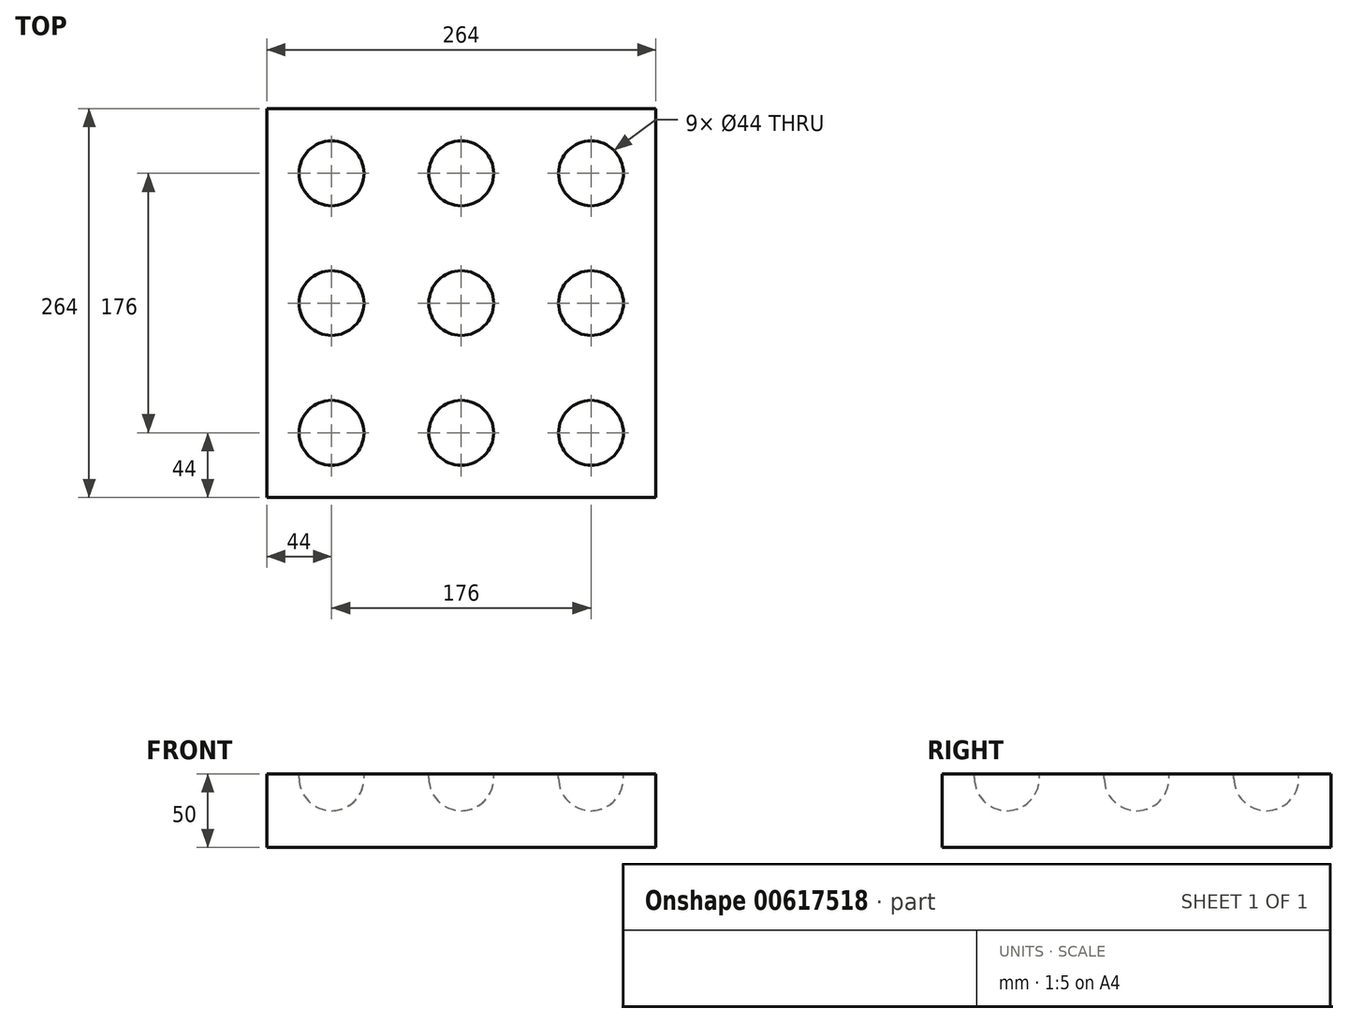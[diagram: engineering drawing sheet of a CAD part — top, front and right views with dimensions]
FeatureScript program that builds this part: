
annotation { "Feature Type Name" : "Feature", "Feature Type Description" : "" }
export const myFeature = defineFeature(function(context is Context, id is Id, definition is map)
    precondition{}
    {
        {
            var Q0;
            Q0=qCreatedBy(makeId("Top.planeOp"),FACE);
            var sketch = newSketch(context, id + "F0", { "sketchPlane" : qUnion([Q0])});
            skPoint(sketch, "E0.middle", {"position": v(0, 0) * mm});
            skPoint(sketch, "E1.middle", {"position": v(-88, 0) * mm});
            skPoint(sketch, "E1.middle.positionSnap0", {"position": v(-22, 0) * mm});
            skPoint(sketch, "E1.centerSnap0", {"position": v(-22, 0) * mm});
            skLineSegment(sketch, "E2.bottom", {"start": v(-132, 132) * mm, "end": v(132, 132) * mm});
            skLineSegment(sketch, "E2.top", {"start": v(-132, -132) * mm, "end": v(132, -132) * mm});
            skLineSegment(sketch, "E2.left", {"start": v(-132, 132) * mm, "end": v(-132, -132) * mm});
            skLineSegment(sketch, "E2.right", {"start": v(132, 132) * mm, "end": v(132, -132) * mm});
            skCircle(sketch, "E3", {"center": v(0, 0) * mm, "radius": 22 * mm});
            skCircle(sketch, "E4", {"center": v(-88, 0) * mm, "radius": 22 * mm});
            skCircle(sketch, "E5", {"center": v(0, 88) * mm, "radius": 22 * mm});
            skCircle(sketch, "E6", {"center": v(-88, 88) * mm, "radius": 22 * mm});
            skSolve(sketch);
        }
        {
            var Q0;
            Q0=makeQuery(id+"F0.imprint","IMPRINT",FACE,{"disambiguationData":[TD([[makeQuery(id+"F0.imprint","IMPRINT",EDGE,{"derivedFrom":sQuery(id+"F0.wireOp",EDGE,"E1.bottom")}),-1.0]])]});
            var Q1;
            Q1=makeQuery(id+"F0.imprint","IMPRINT",FACE,{"disambiguationData":[TD([[makeQuery(id+"F0.imprint","IMPRINT",EDGE,{"derivedFrom":sQuery(id+"F0.wireOp",EDGE,"49fc6d9a-2f63-45aa-8606-494b59f81d4b.bottom")}),-1.0]])]});
            var Q2;
            Q2=makeQuery(id+"F0.imprint","IMPRINT",FACE,{"disambiguationData":[TD([[makeQuery(id+"F0.imprint","IMPRINT",EDGE,{"derivedFrom":sQuery(id+"F0.wireOp",EDGE,"1224e65a-86fc-4fc7-9fbe-4337cff8a24c.bottom")}),-1.0]])]});
            var Q3;
            Q3=makeQuery(id+"F0.imprint","IMPRINT",FACE,{"disambiguationData":[TD([[makeQuery(id+"F0.imprint","IMPRINT",EDGE,{"derivedFrom":sQuery(id+"F0.wireOp",EDGE,"E0.bottom")}),-1.0]])]});
            var Q4;
            Q4=makeQuery(id+"F0.imprint","IMPRINT",FACE,{"disambiguationData":[TD([[makeQuery(id+"F0.imprint","IMPRINT",EDGE,{"derivedFrom":sQuery(id+"F0.wireOp",EDGE,"E6")}),1.0]])]});
            var Q5;
            Q5=makeQuery(id+"F0.imprint","IMPRINT",FACE,{"disambiguationData":[TD([[makeQuery(id+"F0.imprint","IMPRINT",EDGE,{"derivedFrom":sQuery(id+"F0.wireOp",EDGE,"E5")}),1.0]])]});
            var Q6;
            Q6=makeQuery(id+"F0.imprint","IMPRINT",FACE,{"disambiguationData":[TD([[makeQuery(id+"F0.imprint","IMPRINT",EDGE,{"derivedFrom":sQuery(id+"F0.wireOp",EDGE,"E4")}),1.0]])]});
            var Q7;
            Q7=makeQuery(id+"F0.imprint","IMPRINT",FACE,{"disambiguationData":[TD([[makeQuery(id+"F0.imprint","IMPRINT",EDGE,{"derivedFrom":sQuery(id+"F0.wireOp",EDGE,"E3")}),1.0]])]});
            extrude(context, id + "F1", {"entities" : qUnion([Q0, Q1, Q2, Q3, Q4, Q5, Q6, Q7]), "oppositeDirection" : true, "depth" : 25 * mm, "offsetDistance" : 25 * mm});
        }
        {
            var Q0;
            Q0=makeQuery(id+"F1.opExtrude","SWEPT_BODY",BODY,{"disambiguationData":[OSD([sQuery(id+"F0.wireOp",EDGE,"E1.bottom"),sQuery(id+"F0.wireOp",EDGE,"E1.top"),sQuery(id+"F0.wireOp",EDGE,"E1.left"),sQuery(id+"F0.wireOp",EDGE,"E1.right")])]});
            var Q1;
            Q1=makeQuery(id+"F1.opExtrude","SWEPT_BODY",BODY,{"disambiguationData":[OSD([sQuery(id+"F0.wireOp",EDGE,"49fc6d9a-2f63-45aa-8606-494b59f81d4b.bottom"),sQuery(id+"F0.wireOp",EDGE,"49fc6d9a-2f63-45aa-8606-494b59f81d4b.top"),sQuery(id+"F0.wireOp",EDGE,"49fc6d9a-2f63-45aa-8606-494b59f81d4b.left"),sQuery(id+"F0.wireOp",EDGE,"49fc6d9a-2f63-45aa-8606-494b59f81d4b.right")])]});
            var Q2;
            Q2=makeQuery(id+"F1.opExtrude","SWEPT_BODY",BODY,{"disambiguationData":[OSD([sQuery(id+"F0.wireOp",EDGE,"E5")])]});
            var Q3;
            Q3=makeQuery(id+"F1.opExtrude","SWEPT_BODY",BODY,{"disambiguationData":[OSD([sQuery(id+"F0.wireOp",EDGE,"E6")])]});
            var Q4;
            Q4=makeQuery(id+"F1.opExtrude","SWEPT_BODY",BODY,{"disambiguationData":[OSD([sQuery(id+"F0.wireOp",EDGE,"E4")])]});
            var Q5;
            Q5=qCreatedBy(makeId("Right.planeOp"),FACE);
            mirror(context, id + "F2", {"entities" : qUnion([Q0, Q1, Q2, Q3, Q4]), "mirrorPlane" : qUnion([Q5])});
        }
        {
            var Q0;
            Q0=makeQuery(id+"F1.opExtrude","SWEPT_BODY",BODY,{"disambiguationData":[OSD([sQuery(id+"F0.wireOp",EDGE,"49fc6d9a-2f63-45aa-8606-494b59f81d4b.bottom"),sQuery(id+"F0.wireOp",EDGE,"49fc6d9a-2f63-45aa-8606-494b59f81d4b.top"),sQuery(id+"F0.wireOp",EDGE,"49fc6d9a-2f63-45aa-8606-494b59f81d4b.left"),sQuery(id+"F0.wireOp",EDGE,"49fc6d9a-2f63-45aa-8606-494b59f81d4b.right")])]});
            var Q1;
            Q1=makeQuery(id+"F1.opExtrude","SWEPT_BODY",BODY,{"disambiguationData":[OSD([sQuery(id+"F0.wireOp",EDGE,"1224e65a-86fc-4fc7-9fbe-4337cff8a24c.bottom"),sQuery(id+"F0.wireOp",EDGE,"1224e65a-86fc-4fc7-9fbe-4337cff8a24c.top"),sQuery(id+"F0.wireOp",EDGE,"1224e65a-86fc-4fc7-9fbe-4337cff8a24c.left"),sQuery(id+"F0.wireOp",EDGE,"1224e65a-86fc-4fc7-9fbe-4337cff8a24c.right")])]});
            var Q2;
            Q2=makeQuery(id+"F2.opPattern","COPY",BODY,{"derivedFrom":makeQuery(id+"F1.opExtrude","SWEPT_BODY",BODY,{"disambiguationData":[OSD([sQuery(id+"F0.wireOp",EDGE,"49fc6d9a-2f63-45aa-8606-494b59f81d4b.bottom"),sQuery(id+"F0.wireOp",EDGE,"49fc6d9a-2f63-45aa-8606-494b59f81d4b.top"),sQuery(id+"F0.wireOp",EDGE,"49fc6d9a-2f63-45aa-8606-494b59f81d4b.left"),sQuery(id+"F0.wireOp",EDGE,"49fc6d9a-2f63-45aa-8606-494b59f81d4b.right")])]}),"instanceName":"1"});
            var Q3;
            Q3=makeQuery(id+"F1.opExtrude","SWEPT_BODY",BODY,{"disambiguationData":[OSD([sQuery(id+"F0.wireOp",EDGE,"E6")])]});
            var Q4;
            Q4=makeQuery(id+"F1.opExtrude","SWEPT_BODY",BODY,{"disambiguationData":[OSD([sQuery(id+"F0.wireOp",EDGE,"E5")])]});
            var Q5;
            Q5=makeQuery(id+"F2.opPattern","COPY",BODY,{"derivedFrom":makeQuery(id+"F1.opExtrude","SWEPT_BODY",BODY,{"disambiguationData":[OSD([sQuery(id+"F0.wireOp",EDGE,"E6")])]}),"instanceName":"1"});
            var Q6;
            Q6=qCreatedBy(makeId("Front.planeOp"),FACE);
            mirror(context, id + "F3", {"entities" : qUnion([Q0, Q1, Q2, Q3, Q4, Q5]), "mirrorPlane" : qUnion([Q6])});
        }
        {
            var Q0;
            Q0=makeQuery(id+"F0.imprint","IMPRINT",FACE,{"disambiguationData":[TD([[makeQuery(id+"F0.imprint","IMPRINT",EDGE,{"derivedFrom":sQuery(id+"F0.wireOp",EDGE,"E4")}),1.0]])]});
            var Q1;
            Q1=makeQuery(id+"F0.imprint","IMPRINT",FACE,{"disambiguationData":[TD([[makeQuery(id+"F0.imprint","IMPRINT",EDGE,{"derivedFrom":sQuery(id+"F0.wireOp",EDGE,"E6")}),1.0]])]});
            var Q2;
            Q2=makeQuery(id+"F0.imprint","IMPRINT",FACE,{"disambiguationData":[TD([[makeQuery(id+"F0.imprint","IMPRINT",EDGE,{"derivedFrom":sQuery(id+"F0.wireOp",EDGE,"E5")}),1.0]])]});
            var Q3;
            Q3=makeQuery(id+"F0.imprint","IMPRINT",FACE,{"disambiguationData":[TD([[makeQuery(id+"F0.imprint","IMPRINT",EDGE,{"derivedFrom":sQuery(id+"F0.wireOp",EDGE,"E3")}),1.0]])]});
            var Q4;
            Q4=makeQuery(id+"F0.imprint","IMPRINT",FACE,{"disambiguationData":[TD([[makeQuery(id+"F0.imprint","IMPRINT",EDGE,{"derivedFrom":sQuery(id+"F0.wireOp",EDGE,"E2.bottom")}),-1.0]])]});
            extrude(context, id + "F4", {"entities" : qUnion([Q0, Q1, Q2, Q3, Q4]), "oppositeDirection" : true, "depth" : 50 * mm, "offsetDistance" : 25 * mm});
        }
        {
            var Q0;
            Q0=makeQuery(id+"F1.opExtrude","SWEPT_BODY",BODY,{"disambiguationData":[OSD([sQuery(id+"F0.wireOp",EDGE,"E3")])]});
            var Q1;
            Q1=makeQuery(id+"F1.opExtrude","SWEPT_BODY",BODY,{"disambiguationData":[OSD([sQuery(id+"F0.wireOp",EDGE,"E5")])]});
            var Q2;
            Q2=makeQuery(id+"F1.opExtrude","SWEPT_BODY",BODY,{"disambiguationData":[OSD([sQuery(id+"F0.wireOp",EDGE,"E4")])]});
            var Q3;
            Q3=makeQuery(id+"F1.opExtrude","SWEPT_BODY",BODY,{"disambiguationData":[OSD([sQuery(id+"F0.wireOp",EDGE,"E6")])]});
            var Q4;
            Q4=makeQuery(id+"F2.opPattern","COPY",BODY,{"derivedFrom":makeQuery(id+"F1.opExtrude","SWEPT_BODY",BODY,{"disambiguationData":[OSD([sQuery(id+"F0.wireOp",EDGE,"E4")])]}),"instanceName":"1"});
            var Q5;
            Q5=makeQuery(id+"F2.opPattern","COPY",BODY,{"derivedFrom":makeQuery(id+"F1.opExtrude","SWEPT_BODY",BODY,{"disambiguationData":[OSD([sQuery(id+"F0.wireOp",EDGE,"E5")])]}),"instanceName":"1"});
            var Q6;
            Q6=makeQuery(id+"F2.opPattern","COPY",BODY,{"derivedFrom":makeQuery(id+"F1.opExtrude","SWEPT_BODY",BODY,{"disambiguationData":[OSD([sQuery(id+"F0.wireOp",EDGE,"E6")])]}),"instanceName":"1"});
            var Q7;
            Q7=makeQuery(id+"F3.opPattern","COPY",BODY,{"derivedFrom":makeQuery(id+"F1.opExtrude","SWEPT_BODY",BODY,{"disambiguationData":[OSD([sQuery(id+"F0.wireOp",EDGE,"E5")])]}),"instanceName":"1"});
            var Q8;
            Q8=makeQuery(id+"F3.opPattern","COPY",BODY,{"derivedFrom":makeQuery(id+"F1.opExtrude","SWEPT_BODY",BODY,{"disambiguationData":[OSD([sQuery(id+"F0.wireOp",EDGE,"E6")])]}),"instanceName":"1"});
            var Q9;
            Q9=makeQuery(id+"F3.opPattern","COPY",BODY,{"derivedFrom":makeQuery(id+"F2.opPattern","COPY",BODY,{"derivedFrom":makeQuery(id+"F1.opExtrude","SWEPT_BODY",BODY,{"disambiguationData":[OSD([sQuery(id+"F0.wireOp",EDGE,"E6")])]}),"instanceName":"1"}),"instanceName":"1"});
            var Q10;
            Q10=makeQuery(id+"F4.opExtrude","SWEPT_BODY",BODY,{"disambiguationData":[OSD([sQuery(id+"F0.wireOp",EDGE,"E2.bottom"),sQuery(id+"F0.wireOp",EDGE,"E2.top"),sQuery(id+"F0.wireOp",EDGE,"E2.left"),sQuery(id+"F0.wireOp",EDGE,"E2.right")])]});
            booleanBodies(context, id + "F5", {"operationType" : BooleanOperationType.SUBTRACTION, "tools" : qUnion([Q0, Q1, Q2, Q3, Q4, Q5, Q6, Q7, Q8, Q9]), "targets" : qUnion([Q10])});
        }
        {
            var Q0;
            Q0=makeQuery(id+"F5.opBoolean","COPY",FACE,{"derivedFrom":makeQuery(id+"F1.opExtrude","CAP_FACE",FACE,{"disambiguationData":[OSD([sQuery(id+"F0.wireOp",EDGE,"E6")])],"isStart":false})});
            var Q1;
            Q1=makeQuery(id+"F5.opBoolean","COPY",FACE,{"derivedFrom":makeQuery(id+"F1.opExtrude","CAP_FACE",FACE,{"disambiguationData":[OSD([sQuery(id+"F0.wireOp",EDGE,"E4")])],"isStart":false})});
            var Q2;
            Q2=makeQuery(id+"F5.opBoolean","COPY",FACE,{"derivedFrom":makeQuery(id+"F1.opExtrude","CAP_FACE",FACE,{"disambiguationData":[OSD([sQuery(id+"F0.wireOp",EDGE,"E3")])],"isStart":false})});
            var Q3;
            Q3=makeQuery(id+"F5.opBoolean","COPY",FACE,{"derivedFrom":makeQuery(id+"F1.opExtrude","CAP_FACE",FACE,{"disambiguationData":[OSD([sQuery(id+"F0.wireOp",EDGE,"E5")])],"isStart":false})});
            var Q4;
            Q4=makeQuery(id+"F5.opBoolean","COPY",FACE,{"derivedFrom":makeQuery(id+"F2.opPattern","COPY",FACE,{"derivedFrom":makeQuery(id+"F1.opExtrude","CAP_FACE",FACE,{"disambiguationData":[OSD([sQuery(id+"F0.wireOp",EDGE,"E6")])],"isStart":false}),"instanceName":"1"})});
            var Q5;
            Q5=makeQuery(id+"F5.opBoolean","COPY",FACE,{"derivedFrom":makeQuery(id+"F2.opPattern","COPY",FACE,{"derivedFrom":makeQuery(id+"F1.opExtrude","CAP_FACE",FACE,{"disambiguationData":[OSD([sQuery(id+"F0.wireOp",EDGE,"E4")])],"isStart":false}),"instanceName":"1"})});
            var Q6;
            Q6=makeQuery(id+"F5.opBoolean","COPY",FACE,{"derivedFrom":makeQuery(id+"F3.opPattern","COPY",FACE,{"derivedFrom":makeQuery(id+"F2.opPattern","COPY",FACE,{"derivedFrom":makeQuery(id+"F1.opExtrude","CAP_FACE",FACE,{"disambiguationData":[OSD([sQuery(id+"F0.wireOp",EDGE,"E6")])],"isStart":false}),"instanceName":"1"}),"instanceName":"1"})});
            var Q7;
            Q7=makeQuery(id+"F5.opBoolean","COPY",EDGE,{"derivedFrom":makeQuery(id+"F3.opPattern","COPY",EDGE,{"derivedFrom":makeQuery(id+"F1.opExtrude","CAP_EDGE",EDGE,{"disambiguationData":[OSD([sQuery(id+"F0.wireOp",EDGE,"E5")])],"isStart":false}),"instanceName":"1"})});
            var Q8;
            Q8=makeQuery(id+"F5.opBoolean","COPY",FACE,{"derivedFrom":makeQuery(id+"F3.opPattern","COPY",FACE,{"derivedFrom":makeQuery(id+"F1.opExtrude","CAP_FACE",FACE,{"disambiguationData":[OSD([sQuery(id+"F0.wireOp",EDGE,"E6")])],"isStart":false}),"instanceName":"1"})});
            fillet(context, id + "F6", {"entities" : qUnion([Q0, Q1, Q2, Q3, Q4, Q5, Q6, Q7, Q8]), "radius" : 22 * mm, "tangentPropagation" : true, "allowEdgeOverflow" : false});
        }
    });
